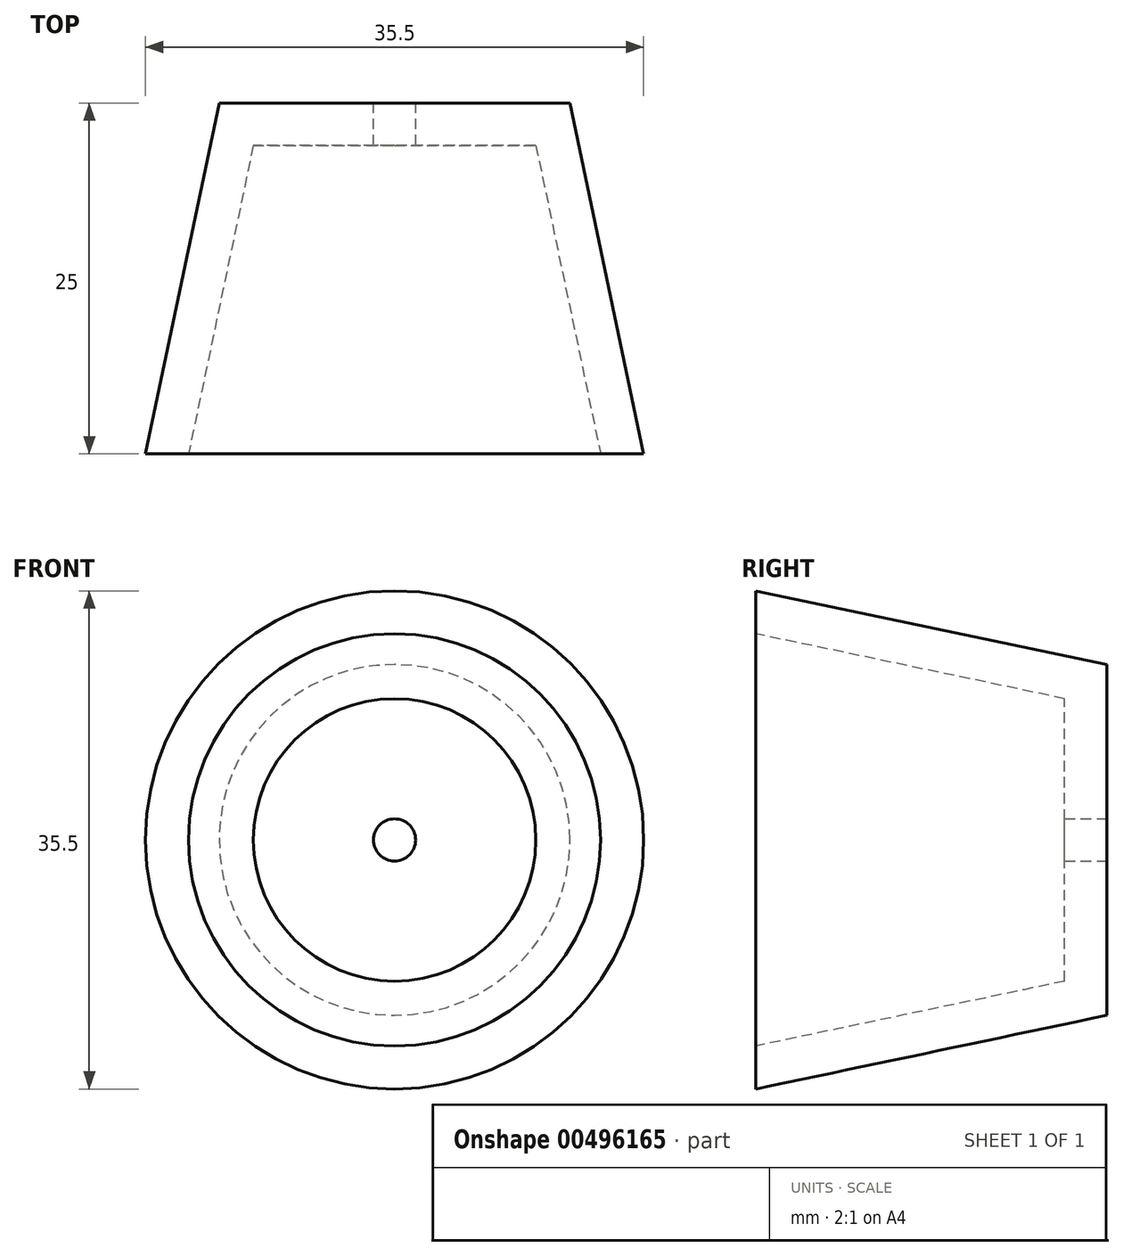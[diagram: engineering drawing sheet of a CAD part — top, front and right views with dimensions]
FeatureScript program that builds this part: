
annotation { "Feature Type Name" : "Feature", "Feature Type Description" : "" }
export const myFeature = defineFeature(function(context is Context, id is Id, definition is map)
    precondition{}
    {
        {
            var Q0;
            Q0=qCreatedBy(makeId("Front.planeOp"),FACE);
            var sketch = newSketch(context, id + "F0", { "sketchPlane" : qUnion([Q0])});
            skCircle(sketch, "E0", {"center": v(0, 0) * mm, "radius": 12.5 * mm});
            skSolve(sketch);
        }
        {
            var Q0;
            Q0=makeQuery(id+"F0.imprint","IMPRINT",FACE,{"disambiguationData":[TD([[makeQuery(id+"F0.imprint","IMPRINT",EDGE,{"derivedFrom":sQuery(id+"F0.wireOp",EDGE,"E0")}),1.0]])]});
            cPlane(context, id + "F1", {"entities" : qUnion([Q0]), "cplaneType" : CPlaneType.OFFSET, "offset" : 25 * mm, "width" : 150 * mm, "height" : 150 * mm});
        }
        {
            var Q0;
            Q0=qCreatedBy(id+"F1.planeOp",FACE);
            var sketch = newSketch(context, id + "F2", { "sketchPlane" : qUnion([Q0])});
            skCircle(sketch, "E1", {"center": v(0, 0) * mm, "radius": 17.75 * mm});
            skSolve(sketch);
        }
        {
            var Q0;
            Q0=makeQuery(id+"F2.imprint","IMPRINT",FACE,{"disambiguationData":[TD([[makeQuery(id+"F2.imprint","IMPRINT",EDGE,{"derivedFrom":sQuery(id+"F2.wireOp",EDGE,"E1")}),1.0]])]});
            var Q1;
            Q1=makeQuery(id+"F0.imprint","IMPRINT",FACE,{"disambiguationData":[TD([[makeQuery(id+"F0.imprint","IMPRINT",EDGE,{"derivedFrom":sQuery(id+"F0.wireOp",EDGE,"E0")}),1.0]])]});
            loft(context, id + "F3", {"sheetProfilesArray" : [{ "sheetProfileEntities" : qUnion([Q0]) }, { "sheetProfileEntities" : qUnion([Q1]) }]});
        }
        {
            var Q0;
            Q0=makeQuery(id+"F3.opLoft","CAP_FACE",FACE,{"disambiguationData":[OSD([makeQuery(id+"F2.imprint","IMPRINT",FACE,{"disambiguationData":[TD([[makeQuery(id+"F2.imprint","IMPRINT",EDGE,{"derivedFrom":sQuery(id+"F2.wireOp",EDGE,"E1")}),1.0]])]})])],"isStart":true});
            shell(context, id + "F4", {"entities" : qUnion([Q0]), "thickness" : 3 * mm});
        }
        {
            var Q0;
            Q0=makeQuery(id+"F3.opLoft","CAP_FACE",FACE,{"disambiguationData":[OSD([makeQuery(id+"F0.imprint","IMPRINT",FACE,{"disambiguationData":[TD([[makeQuery(id+"F0.imprint","IMPRINT",EDGE,{"derivedFrom":sQuery(id+"F0.wireOp",EDGE,"E0")}),1.0]])]})])],"isStart":true});
            cPlane(context, id + "F5", {"entities" : qUnion([Q0]), "cplaneType" : CPlaneType.OFFSET, "offset" : 0 * mm, "width" : 150 * mm, "height" : 150 * mm});
        }
        {
            var Q0;
            Q0=qCreatedBy(id+"F5.planeOp",FACE);
            var sketch = newSketch(context, id + "F6", { "sketchPlane" : qUnion([Q0])});
            skCircle(sketch, "E2", {"center": v(0, 0) * mm, "radius": 1.5 * mm});
            skSolve(sketch);
        }
        {
            var Q0;
            Q0=sQuery(id+"F6.wireOp",VERTEX,"E2.center");
            var Q1;
            Q1=makeQuery(id+"F3.opLoft","SWEPT_BODY",BODY,{"disambiguationData":[OSD([makeQuery(id+"F0.imprint","IMPRINT",FACE,{"disambiguationData":[TD([[makeQuery(id+"F0.imprint","IMPRINT",EDGE,{"derivedFrom":sQuery(id+"F0.wireOp",EDGE,"E0")}),1.0]])]}),makeQuery(id+"F2.imprint","IMPRINT",FACE,{"disambiguationData":[TD([[makeQuery(id+"F2.imprint","IMPRINT",EDGE,{"derivedFrom":sQuery(id+"F2.wireOp",EDGE,"E1")}),1.0]])]})])]});
            hole(context, id + "F7", {"style" : HoleStyle.SIMPLE, "endStyle" : HoleEndStyle.THROUGH, "holeDiameter" : 3 * mm, "isTappedThrough" : true, "tappedDepth" : 12 * mm, "tapClearance" : 3, "locations" : qUnion([Q0]), "scope" : qUnion([Q1])});
        }
        {
            var Q0;
            Q0=makeQuery(id+"F3.opLoft","CAP_FACE",FACE,{"disambiguationData":[OSD([makeQuery(id+"F2.imprint","IMPRINT",FACE,{"disambiguationData":[TD([[makeQuery(id+"F2.imprint","IMPRINT",EDGE,{"derivedFrom":sQuery(id+"F2.wireOp",EDGE,"E1")}),1.0]])]})])],"isStart":true});
            cPlane(context, id + "F8", {"entities" : qUnion([Q0]), "cplaneType" : CPlaneType.OFFSET, "offset" : 7 * mm, "oppositeDirection" : true, "width" : 150 * mm, "height" : 150 * mm});
        }
    });
